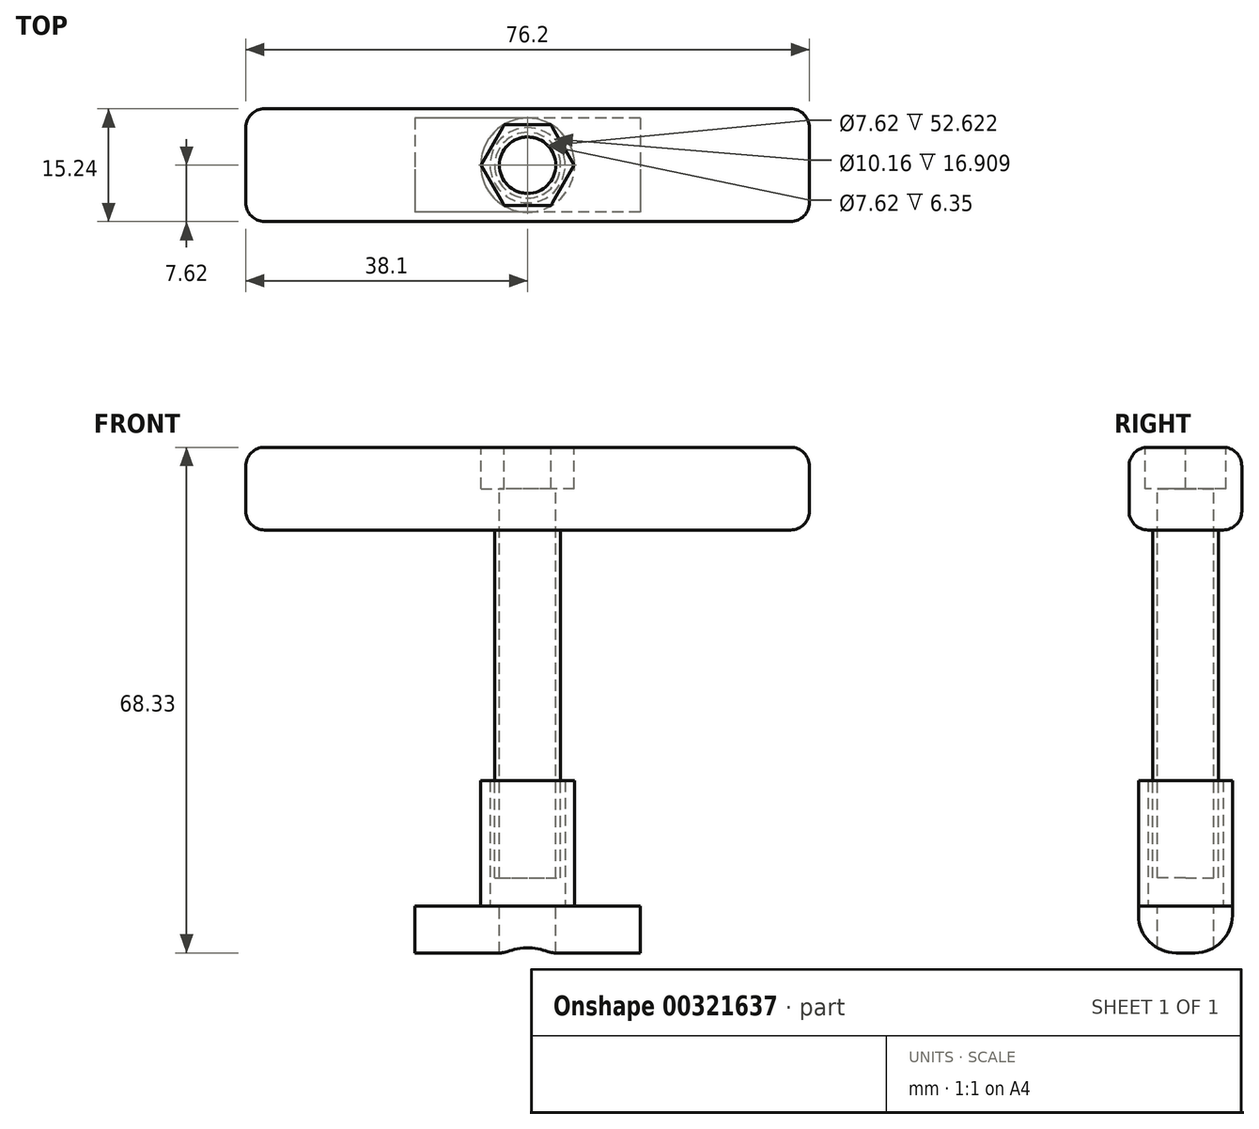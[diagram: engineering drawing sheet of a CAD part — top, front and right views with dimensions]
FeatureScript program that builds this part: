
annotation { "Feature Type Name" : "Feature", "Feature Type Description" : "" }
export const myFeature = defineFeature(function(context is Context, id is Id, definition is map)
    precondition{}
    {
        {
            var Q0;
            Q0=qCreatedBy(makeId("Top.planeOp"),FACE);
            var sketch = newSketch(context, id + "F0", { "sketchPlane" : qUnion([Q0])});
            skLineSegment(sketch, "E0.bottom", {"start": v(38.1, -7.62) * mm, "end": v(-38.1, -7.62) * mm});
            skLineSegment(sketch, "E0.top", {"start": v(38.1, 7.62) * mm, "end": v(-38.1, 7.62) * mm});
            skLineSegment(sketch, "E0.left", {"start": v(38.1, -7.62) * mm, "end": v(38.1, 7.62) * mm});
            skLineSegment(sketch, "E0.right", {"start": v(-38.1, -7.62) * mm, "end": v(-38.1, 7.62) * mm});
            skPoint(sketch, "E0.middle", {"position": v(0, 0) * mm});
            skSolve(sketch);
        }
        {
            var Q0;
            Q0=makeQuery(id+"F0.imprint","IMPRINT",FACE,{"disambiguationData":[TD([[makeQuery(id+"F0.imprint","IMPRINT",EDGE,{"derivedFrom":sQuery(id+"F0.wireOp",EDGE,"E0.bottom")}),-1.0]])]});
            extrude(context, id + "F1", {"entities" : qUnion([Q0]), "depth" : 11.18 * mm});
        }
        {
            var Q0;
            Q0=makeQuery(id+"F1.opExtrude","CAP_FACE",FACE,{"disambiguationData":[OSD([sQuery(id+"F0.wireOp",EDGE,"E0.bottom"),sQuery(id+"F0.wireOp",EDGE,"E0.top"),sQuery(id+"F0.wireOp",EDGE,"E0.left"),sQuery(id+"F0.wireOp",EDGE,"E0.right")])],"isStart":false});
            var sketch = newSketch(context, id + "F2", { "sketchPlane" : qUnion([Q0])});
            skSolve(sketch);
        }
        {
            var Q0;
            Q0=makeQuery(id+"F2.imprint","IMPRINT",FACE,{"disambiguationData":[TD([[makeQuery(id+"F2.imprint","IMPRINT",EDGE,{"derivedFrom":makeQuery(id+"F1.opExtrude","CAP_EDGE",EDGE,{"disambiguationData":[OSD([sQuery(id+"F0.wireOp",EDGE,"E0.bottom")])],"isStart":false})}),-1.0]])]});
            var sketch = newSketch(context, id + "F3", { "sketchPlane" : qUnion([Q0])});
            skCircle(sketch, "E1.cCircle", {"center": v(0, 0) * mm, "radius": 5.46 * mm, "construction": true});
            skLineSegment(sketch, "E1.0", {"start": v(3.15, -5.46) * mm, "end": v(-3.15, -5.46) * mm});
            skLineSegment(sketch, "E1.1", {"start": v(-3.15, -5.46) * mm, "end": v(-6.3, 0) * mm});
            skLineSegment(sketch, "E1.2", {"start": v(-6.3, 0) * mm, "end": v(-3.15, 5.46) * mm});
            skLineSegment(sketch, "E1.3", {"start": v(-3.15, 5.46) * mm, "end": v(3.15, 5.46) * mm});
            skLineSegment(sketch, "E1.4", {"start": v(3.15, 5.46) * mm, "end": v(6.3, 0) * mm});
            skLineSegment(sketch, "E1.5", {"start": v(6.3, 0) * mm, "end": v(3.15, -5.46) * mm});
            skPoint(sketch, "E1.0.midPoint", {"position": v(0, -5.46) * mm});
            skSolve(sketch);
        }
        {
            var Q0;
            Q0 = qSketchRegion(id + "F3", true);
            extrude(context, id + "F4", {"entities" : qUnion([Q0]), "operationType" : NewBodyOperationType.REMOVE, "oppositeDirection" : true, "depth" : 5.6 * mm});
        }
        {
            var Q0;
            Q0=makeQuery(id+"F2.imprint","IMPRINT",FACE,{"disambiguationData":[TD([[makeQuery(id+"F2.imprint","IMPRINT",EDGE,{"derivedFrom":makeQuery(id+"F1.opExtrude","CAP_EDGE",EDGE,{"disambiguationData":[OSD([sQuery(id+"F0.wireOp",EDGE,"E0.bottom")])],"isStart":false})}),-1.0]])]});
            var sketch = newSketch(context, id + "F5", { "sketchPlane" : qUnion([Q0])});
            skCircle(sketch, "E2", {"center": v(0, 0) * mm, "radius": 3.18 * mm});
            skSolve(sketch);
        }
        {
            var Q0;
            Q0 = qSketchRegion(id + "F5", true);
            extrude(context, id + "F6", {"entities" : qUnion([Q0]), "operationType" : NewBodyOperationType.REMOVE, "oppositeDirection" : true, "depth" : 11.18 * mm});
        }
        {
            var Q0;
            Q0=makeQuery(id+"F1.opExtrude","SWEPT_EDGE",EDGE,{"disambiguationData":[OSD([sQuery(id+"F0.wireOp",EDGE,"E0.bottom"),sQuery(id+"F0.wireOp",EDGE,"E0.right")])]});
            var Q1;
            Q1=makeQuery(id+"F1.opExtrude","SWEPT_EDGE",EDGE,{"disambiguationData":[OSD([sQuery(id+"F0.wireOp",EDGE,"E0.top"),sQuery(id+"F0.wireOp",EDGE,"E0.right")])]});
            var Q2;
            Q2=makeQuery(id+"F1.opExtrude","CAP_EDGE",EDGE,{"disambiguationData":[OSD([sQuery(id+"F0.wireOp",EDGE,"E0.left")])],"isStart":true});
            var Q3;
            Q3=makeQuery(id+"F1.opExtrude","SWEPT_EDGE",EDGE,{"disambiguationData":[OSD([sQuery(id+"F0.wireOp",EDGE,"E0.top"),sQuery(id+"F0.wireOp",EDGE,"E0.left")])]});
            var Q4;
            Q4=makeQuery(id+"F1.opExtrude","CAP_EDGE",EDGE,{"disambiguationData":[OSD([sQuery(id+"F0.wireOp",EDGE,"E0.top")])],"isStart":false});
            var Q5;
            Q5=makeQuery(id+"F1.opExtrude","CAP_EDGE",EDGE,{"disambiguationData":[OSD([sQuery(id+"F0.wireOp",EDGE,"E0.top")])],"isStart":true});
            var Q6;
            Q6=makeQuery(id+"F1.opExtrude","CAP_EDGE",EDGE,{"disambiguationData":[OSD([sQuery(id+"F0.wireOp",EDGE,"E0.right")])],"isStart":false});
            var Q7;
            Q7=makeQuery(id+"F1.opExtrude","CAP_EDGE",EDGE,{"disambiguationData":[OSD([sQuery(id+"F0.wireOp",EDGE,"E0.right")])],"isStart":true});
            var Q8;
            Q8=makeQuery(id+"F1.opExtrude","CAP_EDGE",EDGE,{"disambiguationData":[OSD([sQuery(id+"F0.wireOp",EDGE,"E0.bottom")])],"isStart":true});
            var Q9;
            Q9=makeQuery(id+"F1.opExtrude","CAP_EDGE",EDGE,{"disambiguationData":[OSD([sQuery(id+"F0.wireOp",EDGE,"E0.left")])],"isStart":false});
            var Q10;
            Q10=makeQuery(id+"F1.opExtrude","CAP_EDGE",EDGE,{"disambiguationData":[OSD([sQuery(id+"F0.wireOp",EDGE,"E0.bottom")])],"isStart":false});
            var Q11;
            Q11=makeQuery(id+"F1.opExtrude","SWEPT_EDGE",EDGE,{"disambiguationData":[OSD([sQuery(id+"F0.wireOp",EDGE,"E0.bottom"),sQuery(id+"F0.wireOp",EDGE,"E0.left")])]});
            fillet(context, id + "F7", {"entities" : qUnion([Q0, Q1, Q2, Q3, Q4, Q5, Q6, Q7, Q8, Q9, Q10, Q11]), "radius" : 2.54 * mm, "tangentPropagation" : true, "allowEdgeOverflow" : false});
        }
        {
            var Q0;
            Q0=makeQuery(id+"F1.opExtrude","CAP_FACE",FACE,{"disambiguationData":[OSD([sQuery(id+"F0.wireOp",EDGE,"E0.bottom"),sQuery(id+"F0.wireOp",EDGE,"E0.top"),sQuery(id+"F0.wireOp",EDGE,"E0.left"),sQuery(id+"F0.wireOp",EDGE,"E0.right")])],"isStart":true});
            var sketch = newSketch(context, id + "F8", { "sketchPlane" : qUnion([Q0])});
            skCircle(sketch, "E3", {"center": v(0, 0) * mm, "radius": 4.45 * mm});
            skSolve(sketch);
        }
        {
            var Q0;
            Q0 = qSketchRegion(id + "F8", true);
            extrude(context, id + "F9", {"entities" : qUnion([Q0]), "operationType" : NewBodyOperationType.ADD, "depth" : 50.8 * mm});
        }
        {
            var Q0;
            Q0=makeQuery(id+"F2.imprint","IMPRINT",FACE,{"disambiguationData":[TD([[makeQuery(id+"F2.imprint","IMPRINT",EDGE,{"derivedFrom":makeQuery(id+"F1.opExtrude","CAP_EDGE",EDGE,{"disambiguationData":[OSD([sQuery(id+"F0.wireOp",EDGE,"E0.bottom")])],"isStart":false})}),-1.0]])]});
            var sketch = newSketch(context, id + "F10", { "sketchPlane" : qUnion([Q0])});
            skCircle(sketch, "E4", {"center": v(0, 0) * mm, "radius": 3.18 * mm});
            skSolve(sketch);
        }
        {
            var Q0;
            Q0 = qSketchRegion(id + "F10", true);
            extrude(context, id + "F11", {"entities" : qUnion([Q0]), "operationType" : NewBodyOperationType.REMOVE, "oppositeDirection" : true, "depth" : 61.98 * mm});
        }
        {
            var Q0;
            Q0=makeQuery(id+"F9.opExtrude","CAP_FACE",FACE,{"disambiguationData":[OSD([sQuery(id+"F8.wireOp",EDGE,"E3")])],"isStart":false});
            var sketch = newSketch(context, id + "F12", { "sketchPlane" : qUnion([Q0])});
            skLineSegment(sketch, "E5.bottom", {"start": v(15.24, -6.35) * mm, "end": v(-15.24, -6.35) * mm});
            skLineSegment(sketch, "E5.top", {"start": v(15.24, 6.35) * mm, "end": v(-15.24, 6.35) * mm});
            skLineSegment(sketch, "E5.left", {"start": v(15.24, -6.35) * mm, "end": v(15.24, 6.35) * mm});
            skLineSegment(sketch, "E5.right", {"start": v(-15.24, -6.35) * mm, "end": v(-15.24, 6.35) * mm});
            skPoint(sketch, "E5.middle", {"position": v(0, 0) * mm});
            skSolve(sketch);
        }
        {
            var Q0;
            Q0 = qSketchRegion(id + "F12", true);
            extrude(context, id + "F13", {"entities" : qUnion([Q0]), "operationType" : NewBodyOperationType.ADD, "depth" : 6.35 * mm});
        }
        {
            var Q0;
            Q0=makeQuery(id+"F13.opExtrude","CAP_EDGE",EDGE,{"disambiguationData":[OSD([sQuery(id+"F12.wireOp",EDGE,"E5.top")])],"isStart":false});
            var Q1;
            Q1=makeQuery(id+"F13.opExtrude","CAP_EDGE",EDGE,{"disambiguationData":[OSD([sQuery(id+"F12.wireOp",EDGE,"E5.bottom")])],"isStart":false});
            fillet(context, id + "F14", {"entities" : qUnion([Q0, Q1]), "radius" : 5.08 * mm, "tangentPropagation" : true, "allowEdgeOverflow" : false});
        }
        {
            var Q0;
            Q0=makeQuery(id+"F2.imprint","IMPRINT",FACE,{"disambiguationData":[TD([[makeQuery(id+"F2.imprint","IMPRINT",EDGE,{"derivedFrom":makeQuery(id+"F1.opExtrude","CAP_EDGE",EDGE,{"disambiguationData":[OSD([sQuery(id+"F0.wireOp",EDGE,"E0.bottom")])],"isStart":false})}),-1.0]])]});
            var sketch = newSketch(context, id + "F15", { "sketchPlane" : qUnion([Q0])});
            skCircle(sketch, "E6", {"center": v(0, 0) * mm, "radius": 3.18 * mm});
            skSolve(sketch);
        }
        {
            var Q0;
            Q0 = qSketchRegion(id + "F15", true);
            extrude(context, id + "F16", {"entities" : qUnion([Q0]), "operationType" : NewBodyOperationType.REMOVE, "oppositeDirection" : true, "depth" : 71.6 * mm});
        }
        {
            var Q0;
            Q0=makeQuery(id+"F13.opExtrude","SWEPT_FACE",FACE,{"disambiguationData":[OSD([sQuery(id+"F12.wireOp",EDGE,"E5.bottom")])]});
            var sketch = newSketch(context, id + "F17", { "sketchPlane" : qUnion([Q0])});
            skLineSegment(sketch, "E7", {"start": v(-4.7, -50.8) * mm, "end": v(-4.7, -47.03) * mm});
            skLineSegment(sketch, "E8", {"start": v(-4.7, -47.03) * mm, "end": v(5, -47.03) * mm});
            skLineSegment(sketch, "E9", {"start": v(5, -47.03) * mm, "end": v(5, -50.8) * mm});
            skLineSegment(sketch, "E10", {"start": v(5, -50.8) * mm, "end": v(-4.7, -50.8) * mm});
            skSolve(sketch);
        }
        {
            var Q0;
            Q0 = qSketchRegion(id + "F17", true);
            extrude(context, id + "F18", {"entities" : qUnion([Q0]), "operationType" : NewBodyOperationType.REMOVE, "oppositeDirection" : true, "depth" : 16.93 * mm});
        }
        {
            var Q0;
            {var subQ0=sQuery(id+"F12.wireOp",EDGE,"E5.left");var subQ1=sQuery(id+"F12.wireOp",EDGE,"E5.top");var subQ2=sQuery(id+"F12.wireOp",EDGE,"E5.bottom");var subQ3=sQuery(id+"F12.wireOp",EDGE,"E5.right");Q0=makeQuery(id+"F18.boolean.opBoolean","MERGE",FACE,{"derivedFrom":[makeQuery(id+"F13.boolean.opBoolean","SPLIT",FACE,{"disambiguationData":[TD([makeQuery(id+"F9.opExtrude","SWEPT_FACE",FACE,{"disambiguationData":[OSD([sQuery(id+"F8.wireOp",EDGE,"E3")])]})])],"derivedFrom":makeQuery(id+"F13.opExtrude","CAP_FACE",FACE,{"disambiguationData":[OSD([subQ2,subQ1,subQ0,subQ3])],"isStart":true})}),makeQuery(id+"F18.opExtrude","SWEPT_FACE",FACE,{"disambiguationData":[OSD([sQuery(id+"F17.wireOp",EDGE,"E10")])]})]});}
            var sketch = newSketch(context, id + "F19", { "sketchPlane" : qUnion([Q0])});
            skCircle(sketch, "E11", {"center": v(0, 0) * mm, "radius": 5.08 * mm});
            skSolve(sketch);
        }
        {
            var Q0;
            Q0=makeQuery(id+"F19.imprint","IMPRINT",FACE,{"disambiguationData":[TD([[makeQuery(id+"F19.imprint","IMPRINT",EDGE,{"derivedFrom":sQuery(id+"F19.wireOp",EDGE,"E11")}),-1.0]])]});
            var sketch = newSketch(context, id + "F20", { "sketchPlane" : qUnion([Q0])});
            skCircle(sketch, "E12", {"center": v(0, 0) * mm, "radius": 6.35 * mm});
            skSolve(sketch);
        }
        {
            var Q0;
            Q0=makeQuery(id+"F20.imprint","IMPRINT",FACE,{"disambiguationData":[TD([[makeQuery(id+"F20.imprint","IMPRINT",EDGE,{"derivedFrom":sQuery(id+"F20.wireOp",EDGE,"E12")}),1.0]])]});
            extrude(context, id + "F21", {"entities" : qUnion([Q0]), "operationType" : NewBodyOperationType.ADD, "depth" : 16.9 * mm});
        }
        {
            var Q0;
            Q0=makeQuery(id+"F2.imprint","IMPRINT",FACE,{"disambiguationData":[TD([[makeQuery(id+"F2.imprint","IMPRINT",EDGE,{"derivedFrom":makeQuery(id+"F1.opExtrude","CAP_EDGE",EDGE,{"disambiguationData":[OSD([sQuery(id+"F0.wireOp",EDGE,"E0.bottom")])],"isStart":false})}),-1.0]])]});
            var sketch = newSketch(context, id + "F22", { "sketchPlane" : qUnion([Q0])});
            skCircle(sketch, "E13", {"center": v(0, 0) * mm, "radius": 3.8 * mm});
            skSolve(sketch);
        }
        {
            var Q0;
            Q0 = qSketchRegion(id + "F22", true);
            extrude(context, id + "F23", {"entities" : qUnion([Q0]), "operationType" : NewBodyOperationType.REMOVE, "oppositeDirection" : true, "depth" : 111.6 * mm});
        }
    });
